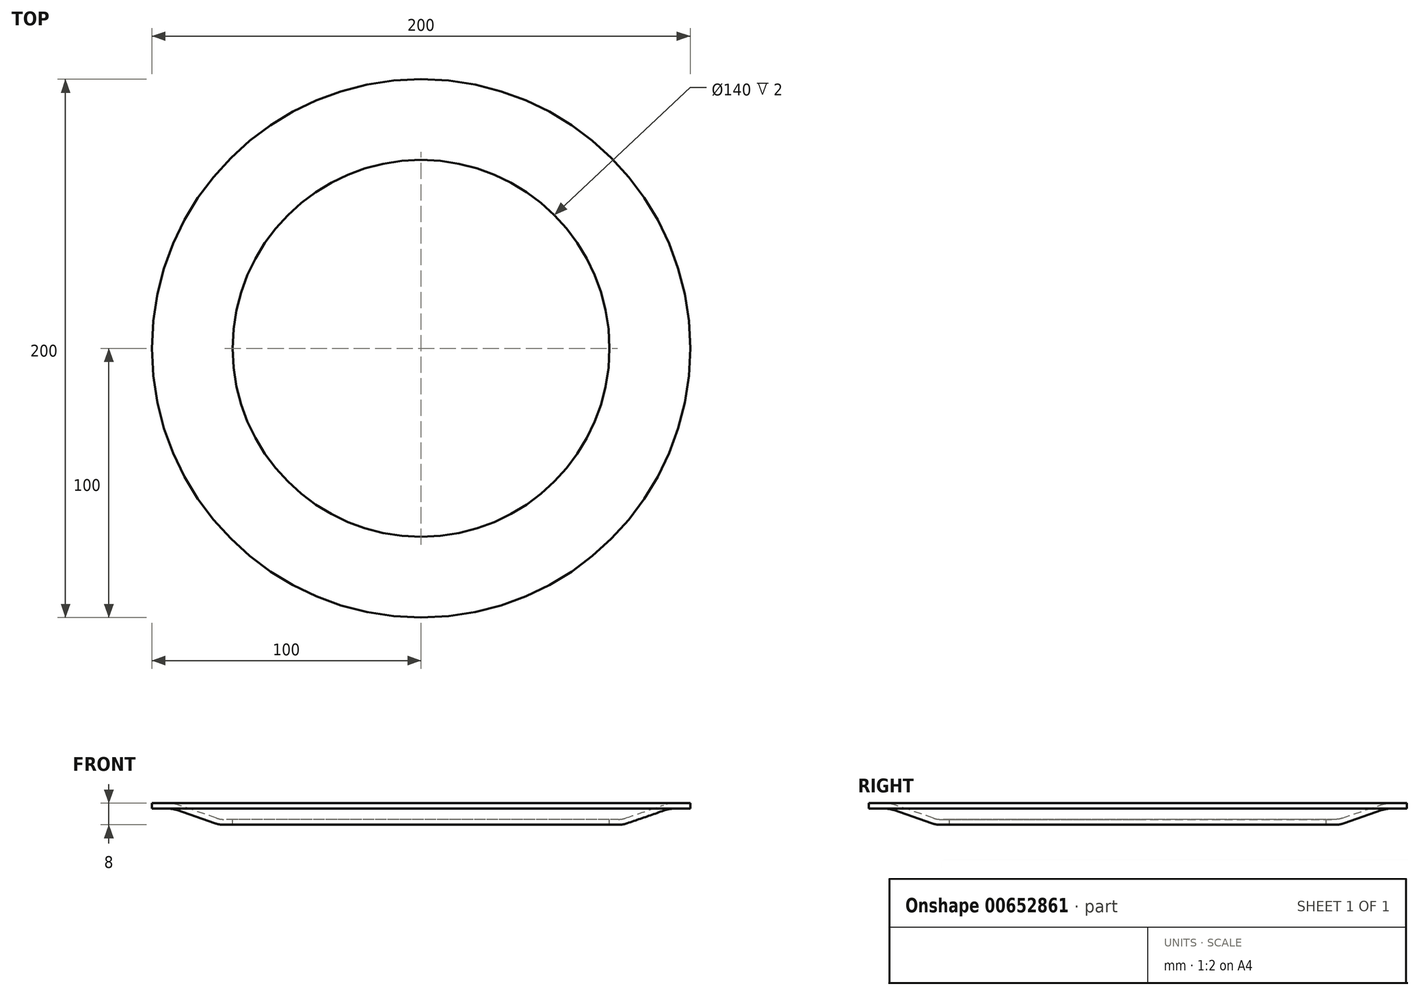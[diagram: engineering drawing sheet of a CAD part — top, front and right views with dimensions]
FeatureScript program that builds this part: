
annotation { "Feature Type Name" : "Feature", "Feature Type Description" : "" }
export const myFeature = defineFeature(function(context is Context, id is Id, definition is map)
    precondition{}
    {
        {
            var Q0;
            Q0=qCreatedBy(makeId("Front.planeOp"),FACE);
            var sketch = newSketch(context, id + "F0", { "sketchPlane" : qUnion([Q0])});
            skLineSegment(sketch, "E0", {"start": v(0, 147.31) * mm, "end": v(0, -139.43) * mm, "construction": true});
            skLineSegment(sketch, "E1", {"start": v(-70, 0) * mm, "end": v(-70, 0) * mm});
            skLineSegment(sketch, "E2", {"start": v(-70, 0) * mm, "end": v(-73.32, 0) * mm});
            skLineSegment(sketch, "E3", {"start": v(-76.6, 0.55) * mm, "end": v(-90.73, 5.45) * mm});
            skLineSegment(sketch, "E4", {"start": v(-94, 6) * mm, "end": v(-100, 6) * mm});
            skPoint(sketch, "E5.visualSharp", {"position": v(-92.32, 6) * mm});
            skArc(sketch, "E5.filletArc", {"start": v(-90.73, 5.45) * mm, "mid": v(-92.34, 5.86) * mm, "end": v(-94, 6) * mm});
            skPoint(sketch, "E6.visualSharp", {"position": v(-75, 0) * mm});
            skArc(sketch, "E6.filletArc", {"start": v(-76.6, 0.55) * mm, "mid": v(-74.98, 0.14) * mm, "end": v(-73.32, 0) * mm});
            skLineSegment(sketch, "E7.0", {"start": v(-94, 8) * mm, "end": v(-100, 8) * mm});
            skLineSegment(sketch, "E7.1", {"start": v(-70, 2) * mm, "end": v(-73.32, 2) * mm});
            skArc(sketch, "E7.2", {"start": v(-75.94, 2.44) * mm, "mid": v(-74.64, 2.11) * mm, "end": v(-73.32, 2) * mm});
            skLineSegment(sketch, "E7.3", {"start": v(-75.94, 2.44) * mm, "end": v(-90.07, 7.34) * mm});
            skArc(sketch, "E7.4", {"start": v(-90.07, 7.34) * mm, "mid": v(-92, 7.83) * mm, "end": v(-94, 8) * mm});
            skLineSegment(sketch, "E8", {"start": v(-100, 8) * mm, "end": v(-100, 6) * mm});
            skLineSegment(sketch, "E9", {"start": v(-70, 2) * mm, "end": v(-70, 0) * mm});
            skSolve(sketch);
        }
        {
            var Q0;
            Q0=makeQuery(id+"F0.imprint","IMPRINT",FACE,{"disambiguationData":[TD([[makeQuery(id+"F0.imprint","IMPRINT",EDGE,{"derivedFrom":sQuery(id+"F0.wireOp",EDGE,"E2")}),-1.0]])]});
            var Q1;
            Q1=sQuery(id+"F0.wireOp",EDGE,"E0");
            revolve(context, id + "F1", {"entities" : qUnion([Q0]), "axis" : qUnion([Q1]), "revolveType" : RevolveType.FULL});
        }
    });
